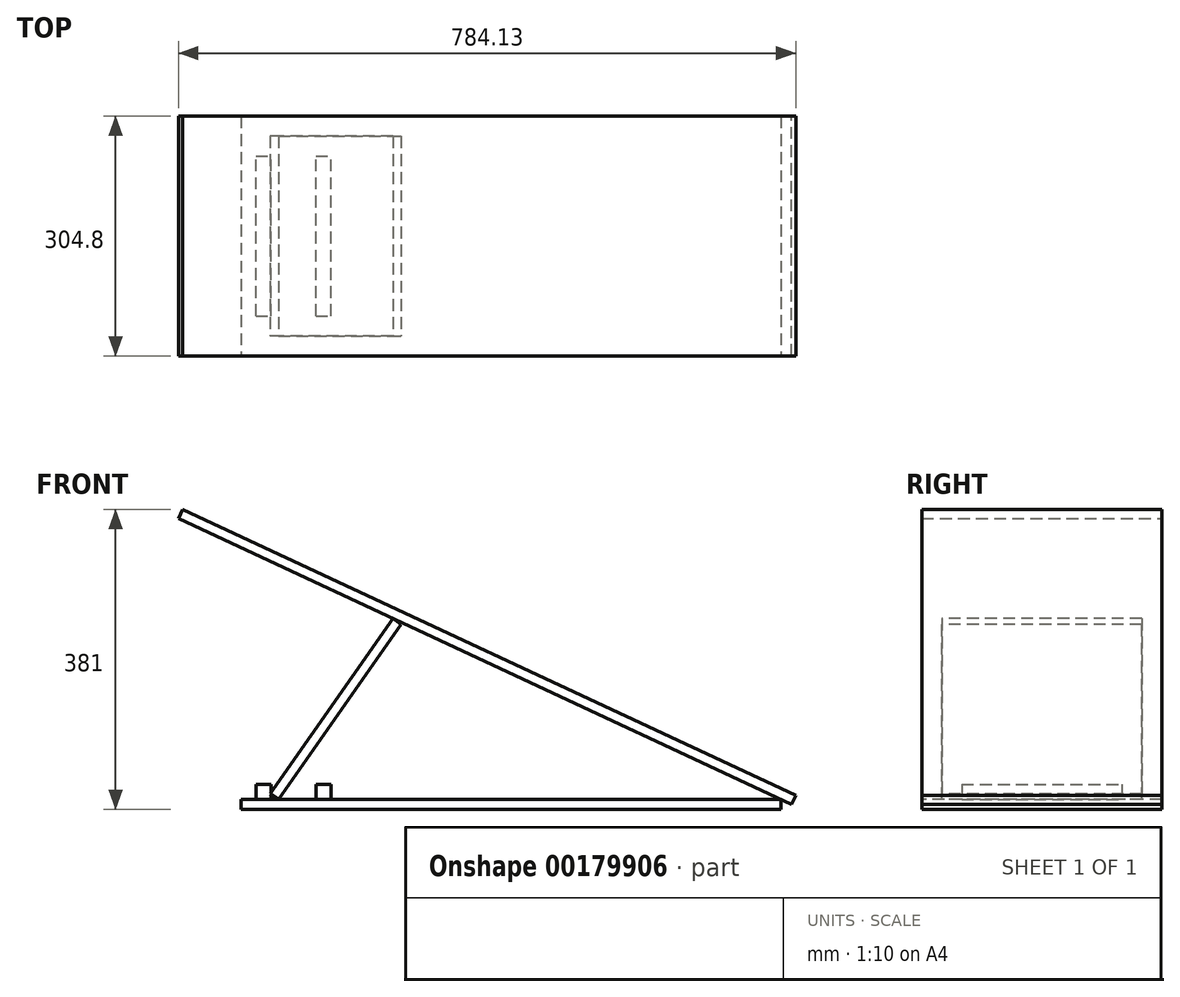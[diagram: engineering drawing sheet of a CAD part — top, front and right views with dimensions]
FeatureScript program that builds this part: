
annotation { "Feature Type Name" : "Feature", "Feature Type Description" : "" }
export const myFeature = defineFeature(function(context is Context, id is Id, definition is map)
    precondition{}
    {
        {
            var Q0;
            Q0=qCreatedBy(makeId("Top.planeOp"),FACE);
            var sketch = newSketch(context, id + "F0", { "sketchPlane" : qUnion([Q0])});
            skLineSegment(sketch, "E0.bottom", {"start": v(-520.75, 152.4) * mm, "end": v(165.05, 152.4) * mm});
            skLineSegment(sketch, "E0.top", {"start": v(-520.75, -152.4) * mm, "end": v(165.05, -152.4) * mm});
            skLineSegment(sketch, "E0.left", {"start": v(-520.75, 152.4) * mm, "end": v(-520.75, -152.4) * mm});
            skLineSegment(sketch, "E0.right", {"start": v(165.05, 152.4) * mm, "end": v(165.05, -152.4) * mm});
            skSolve(sketch);
        }
        {
            var Q0;
            Q0 = qSketchRegion(id + "F0", true);
            extrude(context, id + "F1", {"entities" : qUnion([Q0]), "depth" : 12.7 * mm});
        }
        {
            var Q0;
            Q0=qCreatedBy(makeId("Front.planeOp"),FACE);
            var sketch = newSketch(context, id + "F2", { "sketchPlane" : qUnion([Q0])});
            skLineSegment(sketch, "E1", {"start": v(184.04, 17.86) * mm, "end": v(178.67, 6.35) * mm});
            skLineSegment(sketch, "E2", {"start": v(178.67, 6.35) * mm, "end": v(-600.09, 369.49) * mm});
            skLineSegment(sketch, "E3", {"start": v(-600.09, 369.49) * mm, "end": v(-594.72, 381) * mm});
            skLineSegment(sketch, "E4", {"start": v(-594.72, 381) * mm, "end": v(184.04, 17.86) * mm});
            skSolve(sketch);
        }
        {
            var Q0;
            Q0 = qSketchRegion(id + "F2", true);
            var Q1;
            Q1=makeQuery(id+"F1.opExtrude","SWEPT_FACE",FACE,{"disambiguationData":[OSD([sQuery(id+"F0.wireOp",EDGE,"E0.top")])]});
            var Q2;
            Q2=makeQuery(id+"F1.opExtrude","SWEPT_FACE",FACE,{"disambiguationData":[OSD([sQuery(id+"F0.wireOp",EDGE,"E0.bottom")])]});
            extrude(context, id + "F3", {"entities" : qUnion([Q0]), "endBound" : BoundingType.UP_TO_SURFACE, "endBoundEntityFace" : qUnion([Q1]), "depth" : 25.4 * mm, "hasSecondDirection" : true, "secondDirectionBound" : SecondDirectionBoundingType.UP_TO_SURFACE, "secondDirectionOppositeDirection" : true, "secondDirectionBoundEntityFace" : qUnion([Q2]), "secondDirectionDepth" : 25.4 * mm});
        }
        {
            var Q0;
            Q0=makeQuery(id+"F1.opExtrude","CAP_FACE",FACE,{"disambiguationData":[OSD([sQuery(id+"F0.wireOp",EDGE,"E0.bottom"),sQuery(id+"F0.wireOp",EDGE,"E0.top"),sQuery(id+"F0.wireOp",EDGE,"E0.left"),sQuery(id+"F0.wireOp",EDGE,"E0.right")])],"isStart":false});
            var sketch = newSketch(context, id + "F4", { "sketchPlane" : qUnion([Q0])});
            skLineSegment(sketch, "E5.bottom", {"start": v(-501.7, -101.6) * mm, "end": v(-482.65, -101.6) * mm});
            skLineSegment(sketch, "E5.top", {"start": v(-501.7, 101.6) * mm, "end": v(-482.65, 101.6) * mm});
            skLineSegment(sketch, "E5.left", {"start": v(-501.7, -101.6) * mm, "end": v(-501.7, 101.6) * mm});
            skLineSegment(sketch, "E5.right", {"start": v(-482.65, -101.6) * mm, "end": v(-482.65, 101.6) * mm});
            skLineSegment(sketch, "E6.1.0.0", {"start": v(-406.45, -101.6) * mm, "end": v(-406.45, 101.6) * mm});
            skLineSegment(sketch, "E6.1.0.1", {"start": v(-425.5, -101.6) * mm, "end": v(-406.45, -101.6) * mm});
            skLineSegment(sketch, "E6.1.0.2", {"start": v(-425.5, -101.6) * mm, "end": v(-425.5, 101.6) * mm});
            skLineSegment(sketch, "E6.1.0.3", {"start": v(-425.5, 101.6) * mm, "end": v(-406.45, 101.6) * mm});
            skLineSegment(sketch, "E6.direction1", {"start": v(-482.65, -101.6) * mm, "end": v(-406.45, -101.6) * mm, "construction": true});
            skSolve(sketch);
        }
        {
            var Q0;
            Q0 = qSketchRegion(id + "F4", true);
            extrude(context, id + "F5", {"entities" : qUnion([Q0]), "operationType" : NewBodyOperationType.ADD, "depth" : 19.05 * mm});
        }
        {
            var Q0;
            Q0=qCreatedBy(makeId("Front.planeOp"),FACE);
            var sketch = newSketch(context, id + "F6", { "sketchPlane" : qUnion([Q0])});
            skLineSegment(sketch, "E7", {"start": v(-327.78, 242.5) * mm, "end": v(-317.37, 235.22) * mm});
            skLineSegment(sketch, "E8", {"start": v(-327.78, 242.5) * mm, "end": v(-483.59, 19.98) * mm});
            skLineSegment(sketch, "E9", {"start": v(-473.19, 12.7) * mm, "end": v(-483.59, 19.98) * mm});
            skLineSegment(sketch, "E10", {"start": v(-473.19, 12.7) * mm, "end": v(-317.37, 235.22) * mm});
            skSolve(sketch);
        }
        {
            var Q0;
            Q0=makeQuery(id+"F6.imprint","IMPRINT",FACE,{"disambiguationData":[TD([[makeQuery(id+"F6.imprint","IMPRINT",EDGE,{"derivedFrom":sQuery(id+"F6.wireOp",EDGE,"E7")}),-1.0]])]});
            var Q1;
            Q1=makeQuery(id+"F3.opExtrude","CAP_FACE",FACE,{"disambiguationData":[OSD([sQuery(id+"F2.wireOp",EDGE,"E1"),sQuery(id+"F2.wireOp",EDGE,"E2"),sQuery(id+"F2.wireOp",EDGE,"E3"),sQuery(id+"F2.wireOp",EDGE,"E4")])],"isStart":true});
            var Q2;
            Q2=makeQuery(id+"F3.opExtrude","CAP_FACE",FACE,{"disambiguationData":[OSD([sQuery(id+"F2.wireOp",EDGE,"E1"),sQuery(id+"F2.wireOp",EDGE,"E2"),sQuery(id+"F2.wireOp",EDGE,"E3"),sQuery(id+"F2.wireOp",EDGE,"E4")])],"isStart":false});
            extrude(context, id + "F7", {"entities" : qUnion([Q0]), "oppositeDirection" : true, "endBoundEntityFace" : qUnion([Q1]), "depth" : 127 * mm, "hasSecondDirection" : true, "secondDirectionOppositeDirection" : false, "secondDirectionBoundEntityFace" : qUnion([Q2]), "secondDirectionDepth" : 127 * mm});
        }
    });
